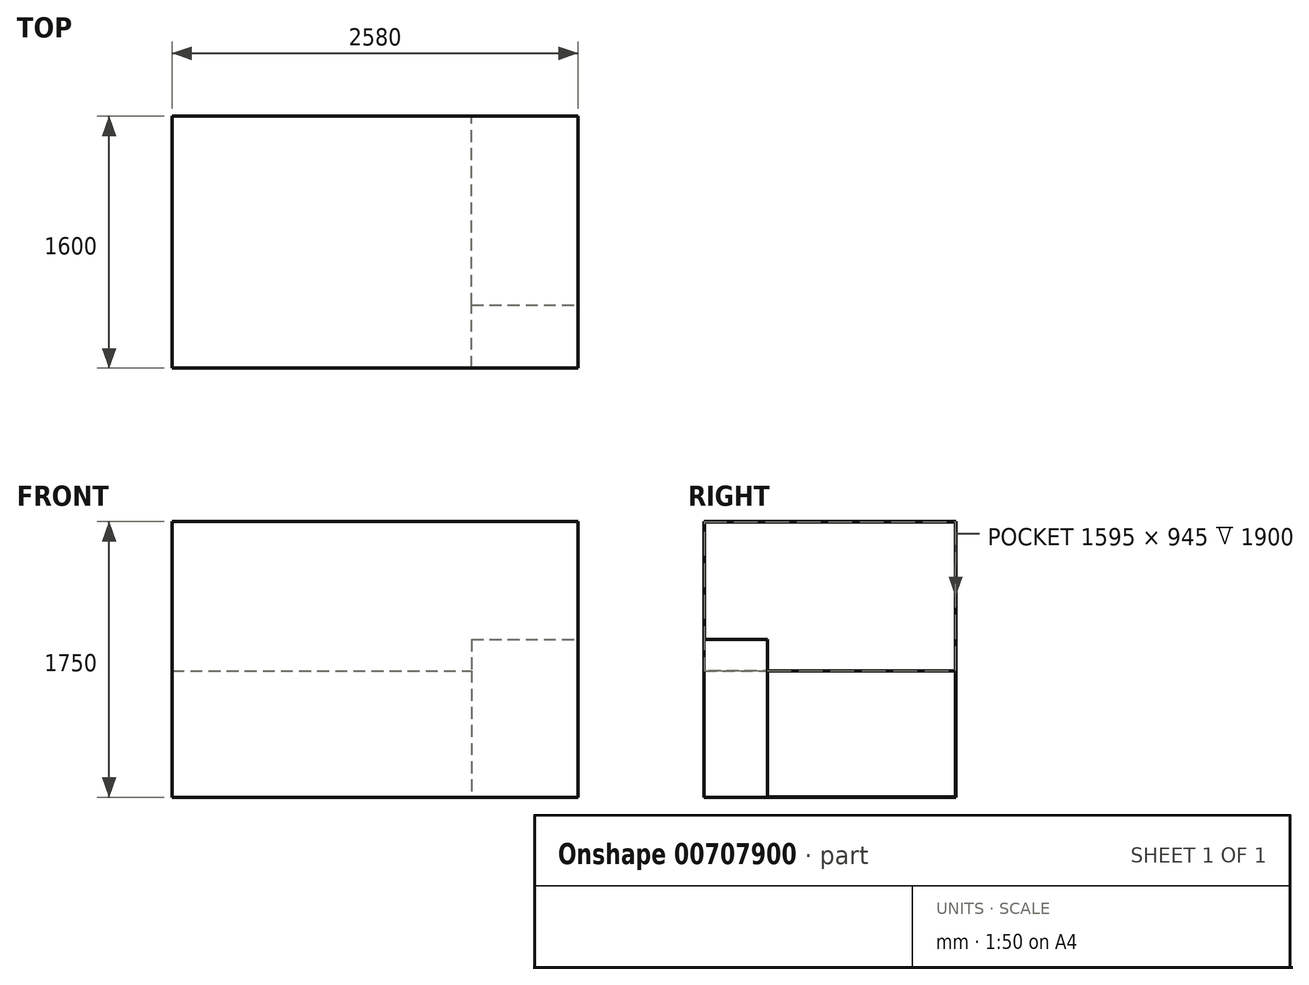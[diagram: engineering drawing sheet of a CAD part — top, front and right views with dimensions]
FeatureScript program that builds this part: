
annotation { "Feature Type Name" : "Feature", "Feature Type Description" : "" }
export const myFeature = defineFeature(function(context is Context, id is Id, definition is map)
    precondition{}
    {
        {
            var Q0;
            Q0=qCreatedBy(makeId("Top.planeOp"),FACE);
            var sketch = newSketch(context, id + "F0", { "sketchPlane" : qUnion([Q0])});
            skLineSegment(sketch, "E0.bottom", {"start": v(0, 0) * mm, "end": v(2580, 0) * mm});
            skLineSegment(sketch, "E0.top", {"start": v(0, -1600) * mm, "end": v(2580, -1600) * mm});
            skLineSegment(sketch, "E0.left", {"start": v(0, 0) * mm, "end": v(0, -1600) * mm});
            skLineSegment(sketch, "E0.right", {"start": v(2580, 0) * mm, "end": v(2580, -1600) * mm});
            skSolve(sketch);
        }
        {
            var Q0;
            Q0 = qSketchRegion(id + "F0", true);
            extrude(context, id + "F1", {"entities" : qUnion([Q0]), "depth" : 1750 * mm, "offsetDistance" : 25 * mm});
        }
        {
            var Q0;
            Q0=makeQuery(id+"F1.opExtrude","SWEPT_FACE",FACE,{"disambiguationData":[OSD([sQuery(id+"F0.wireOp",EDGE,"E0.right")])]});
            shell(context, id + "F2", {"entities" : qUnion([Q0]), "thickness" : 2.5 * mm});
        }
        {
            var Q0;
            {var subQ0=sQuery(id+"F0.wireOp",EDGE,"E0.right");var subQ1=sQuery(id+"F0.wireOp",EDGE,"E0.left");var subQ2=sQuery(id+"F0.wireOp",EDGE,"E0.top");var subQ3=sQuery(id+"F0.wireOp",EDGE,"E0.bottom");Q0=makeQuery(id+"F2.opShell","OFFSET_FACE",FACE,{"disambiguationData":[OSD([subQ3,subQ2,subQ1,subQ0]),TDD([makeQuery(id+"F1.opExtrude","CAP_FACE",FACE,{"disambiguationData":[OSD([subQ3,subQ2,subQ1,subQ0])],"isStart":true})])]});}
            var sketch = newSketch(context, id + "F3", { "sketchPlane" : qUnion([Q0])});
            skLineSegment(sketch, "E1.bottom", {"start": v(2.5, -1597.5) * mm, "end": v(1902.5, -1597.5) * mm});
            skLineSegment(sketch, "E1.top", {"start": v(2.5, -2.5) * mm, "end": v(1902.5, -2.5) * mm});
            skLineSegment(sketch, "E1.left", {"start": v(2.5, -1597.5) * mm, "end": v(2.5, -2.5) * mm});
            skLineSegment(sketch, "E1.right", {"start": v(1902.5, -1597.5) * mm, "end": v(1902.5, -2.5) * mm});
            skSolve(sketch);
        }
        {
            var Q0;
            Q0 = qSketchRegion(id + "F3", true);
            extrude(context, id + "F4", {"entities" : qUnion([Q0]), "operationType" : NewBodyOperationType.ADD, "depth" : 800 * mm, "offsetDistance" : 25 * mm});
        }
        {
            var Q0;
            {var subQ0=sQuery(id+"F0.wireOp",EDGE,"E0.right");var subQ1=sQuery(id+"F0.wireOp",EDGE,"E0.left");var subQ2=sQuery(id+"F0.wireOp",EDGE,"E0.top");var subQ3=sQuery(id+"F0.wireOp",EDGE,"E0.bottom");Q0=makeQuery(id+"F2.opShell","OFFSET_FACE",FACE,{"disambiguationData":[OSD([subQ3,subQ2,subQ1,subQ0]),TDD([makeQuery(id+"F1.opExtrude","CAP_FACE",FACE,{"disambiguationData":[OSD([subQ3,subQ2,subQ1,subQ0])],"isStart":true})])]});}
            var sketch = newSketch(context, id + "F5", { "sketchPlane" : qUnion([Q0])});
            skLineSegment(sketch, "E2.bottom", {"start": v(1902.5, -1597.5) * mm, "end": v(2580, -1597.5) * mm});
            skLineSegment(sketch, "E2.top", {"start": v(1902.5, -1197.5) * mm, "end": v(2580, -1197.5) * mm});
            skLineSegment(sketch, "E2.left", {"start": v(1902.5, -1597.5) * mm, "end": v(1902.5, -1197.5) * mm});
            skLineSegment(sketch, "E2.right", {"start": v(2580, -1597.5) * mm, "end": v(2580, -1197.5) * mm});
            skSolve(sketch);
        }
        {
            var Q0;
            Q0 = qSketchRegion(id + "F5", true);
            extrude(context, id + "F6", {"entities" : qUnion([Q0]), "operationType" : NewBodyOperationType.ADD, "depth" : 1000 * mm, "offsetDistance" : 25 * mm});
        }
    });
